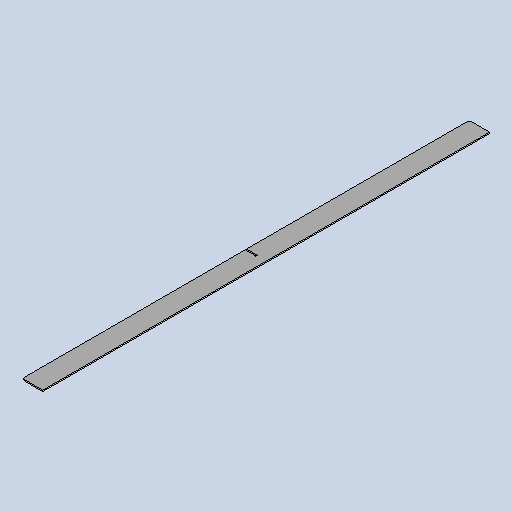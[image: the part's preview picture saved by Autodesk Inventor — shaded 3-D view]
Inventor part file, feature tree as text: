
AUTODESK INVENTOR PART (.ipt)
format: ipt  version: 2025 (Build 290162010, 162A)  size: 104,448 bytes
history: native  units: mm
features: sheet_metal_op x1, chamfer x1, sketch x1, other x1
ambient origin geometry x8: Origin, YZ Plane, XZ Plane, XY Plane, X Axis, Y Axis, Z Axis, Center Point
bodies: Body1 (feature_tree)
feature tree (4):
  sheet_metal_op  "Face2"
  chamfer  "Corner Round1"
  sketch  "Sketch1"  dims[d15=3.0mm d17=1098.0mm d18=50.0mm d19=3.0mm d20=26.0mm d21=6.0mm]
  other  "Plate2"
